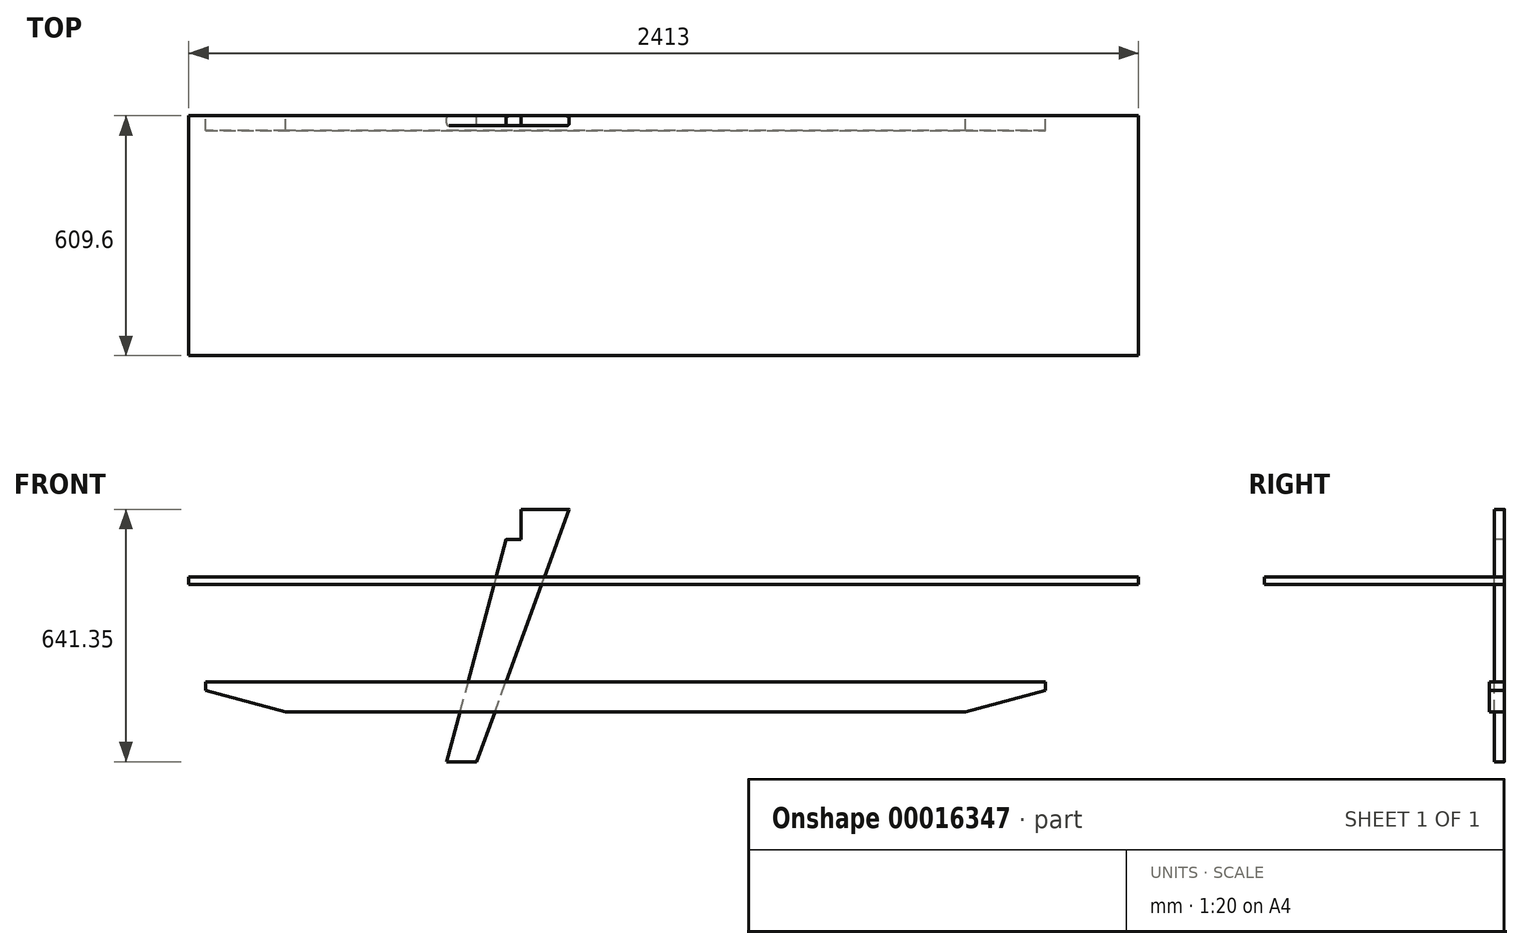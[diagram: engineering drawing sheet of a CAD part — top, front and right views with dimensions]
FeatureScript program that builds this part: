
annotation { "Feature Type Name" : "Feature", "Feature Type Description" : "" }
export const myFeature = defineFeature(function(context is Context, id is Id, definition is map)
    precondition{}
    {
        {
            var Q0;
            Q0=qCreatedBy(makeId("Front.planeOp"),FACE);
            var sketch = newSketch(context, id + "F0", { "sketchPlane" : qUnion([Q0])});
            skLineSegment(sketch, "E0", {"start": v(0, 0) * mm, "end": v(76.2, 0) * mm});
            skLineSegment(sketch, "E1", {"start": v(76.2, 0) * mm, "end": v(311.55, 641.35) * mm});
            skLineSegment(sketch, "E2", {"start": v(311.55, 641.35) * mm, "end": v(171.85, 641.35) * mm});
            skLineSegment(sketch, "E3", {"start": v(171.85, 641.35) * mm, "end": v(0, 0) * mm});
            skSolve(sketch);
        }
        {
            var Q0;
            Q0 = qSketchRegion(id + "F0", true);
            extrude(context, id + "F1", {"entities" : qUnion([Q0]), "depth" : 25.4 * mm});
        }
        {
            var Q0;
            Q0=makeQuery(id+"F1.opExtrude","CAP_EDGE",EDGE,{"disambiguationData":[OSD([sQuery(id+"F0.wireOp",EDGE,"E1")])],"isStart":false});
            var Q1;
            Q1=makeQuery(id+"F1.opExtrude","CAP_EDGE",EDGE,{"disambiguationData":[OSD([sQuery(id+"F0.wireOp",EDGE,"E1")])],"isStart":true});
            var Q2;
            Q2=makeQuery(id+"F1.opExtrude","CAP_EDGE",EDGE,{"disambiguationData":[OSD([sQuery(id+"F0.wireOp",EDGE,"E3")])],"isStart":false});
            var Q3;
            Q3=makeQuery(id+"F1.opExtrude","CAP_EDGE",EDGE,{"disambiguationData":[OSD([sQuery(id+"F0.wireOp",EDGE,"E3")])],"isStart":true});
            fillet(context, id + "F2", {"entities" : qUnion([Q0, Q1, Q2, Q3]), "radius" : 6.35 * mm, "tangentPropagation" : true, "allowEdgeOverflow" : false});
        }
        {
            var Q0;
            Q0=qCreatedBy(makeId("Front.planeOp"),FACE);
            var sketch = newSketch(context, id + "F3", { "sketchPlane" : qUnion([Q0])});
            skLineSegment(sketch, "E4", {"start": v(-612.1, 203.2) * mm, "end": v(1521.5, 203.2) * mm});
            skLineSegment(sketch, "E5", {"start": v(1521.5, 203.2) * mm, "end": v(1521.5, 181.45) * mm});
            skLineSegment(sketch, "E6", {"start": v(1521.5, 181.45) * mm, "end": v(1318.3, 127) * mm});
            skLineSegment(sketch, "E7", {"start": v(1318.3, 127) * mm, "end": v(-408.9, 127) * mm});
            skLineSegment(sketch, "E8", {"start": v(-408.9, 127) * mm, "end": v(-612.1, 181.45) * mm});
            skLineSegment(sketch, "E9", {"start": v(-612.1, 181.45) * mm, "end": v(-612.1, 203.2) * mm});
            skSolve(sketch);
        }
        {
            var Q0;
            Q0 = qSketchRegion(id + "F3", true);
            extrude(context, id + "F4", {"entities" : qUnion([Q0]), "depth" : 38.1 * mm});
        }
        {
            var Q0;
            Q0=qCreatedBy(makeId("Front.planeOp"),FACE);
            var sketch = newSketch(context, id + "F5", { "sketchPlane" : qUnion([Q0])});
            skLineSegment(sketch, "E10.bottom", {"start": v(-654.58, 450.28) * mm, "end": v(1758.42, 450.28) * mm});
            skLineSegment(sketch, "E10.top", {"start": v(-654.58, 469.33) * mm, "end": v(1758.42, 469.33) * mm});
            skLineSegment(sketch, "E10.left", {"start": v(-654.58, 450.28) * mm, "end": v(-654.58, 469.33) * mm});
            skLineSegment(sketch, "E10.right", {"start": v(1758.42, 450.28) * mm, "end": v(1758.42, 469.33) * mm});
            skSolve(sketch);
        }
        {
            var Q0;
            Q0 = qSketchRegion(id + "F5", true);
            extrude(context, id + "F6", {"entities" : qUnion([Q0]), "depth" : 609.6 * mm});
        }
        {
            var Q0;
            Q0=makeQuery(id+"F1.opExtrude","CAP_FACE",FACE,{"disambiguationData":[OSD([sQuery(id+"F0.wireOp",EDGE,"E0"),sQuery(id+"F0.wireOp",EDGE,"E1"),sQuery(id+"F0.wireOp",EDGE,"E2"),sQuery(id+"F0.wireOp",EDGE,"E3")])],"isStart":false});
            var sketch = newSketch(context, id + "F7", { "sketchPlane" : qUnion([Q0])});
            skLineSegment(sketch, "E11.bottom", {"start": v(189.53, 717) * mm, "end": v(101.36, 717) * mm});
            skLineSegment(sketch, "E11.top", {"start": v(189.53, 565.15) * mm, "end": v(151.43, 565.15) * mm});
            skLineSegment(sketch, "E11.left", {"start": v(189.53, 641.35) * mm, "end": v(189.53, 565.15) * mm});
            skLineSegment(sketch, "E12.0", {"start": v(0, 0) * mm, "end": v(171.85, 641.35) * mm, "construction": true});
            skLineSegment(sketch, "E13.0", {"start": v(304.79, 641.35) * mm, "end": v(178.42, 641.35) * mm, "construction": true});
            skLineSegment(sketch, "E14", {"start": v(189.53, 641.35) * mm, "end": v(147.25, 641.35) * mm});
            skLineSegment(sketch, "E15", {"start": v(147.25, 641.35) * mm, "end": v(151.43, 565.15) * mm});
            skSolve(sketch);
        }
        {
            var Q0;
            Q0 = qSketchRegion(id + "F7", true);
            extrude(context, id + "F8", {"entities" : qUnion([Q0]), "operationType" : NewBodyOperationType.REMOVE, "endBound" : BoundingType.THROUGH_ALL, "oppositeDirection" : true, "depth" : 25.4 * mm});
        }
    });
